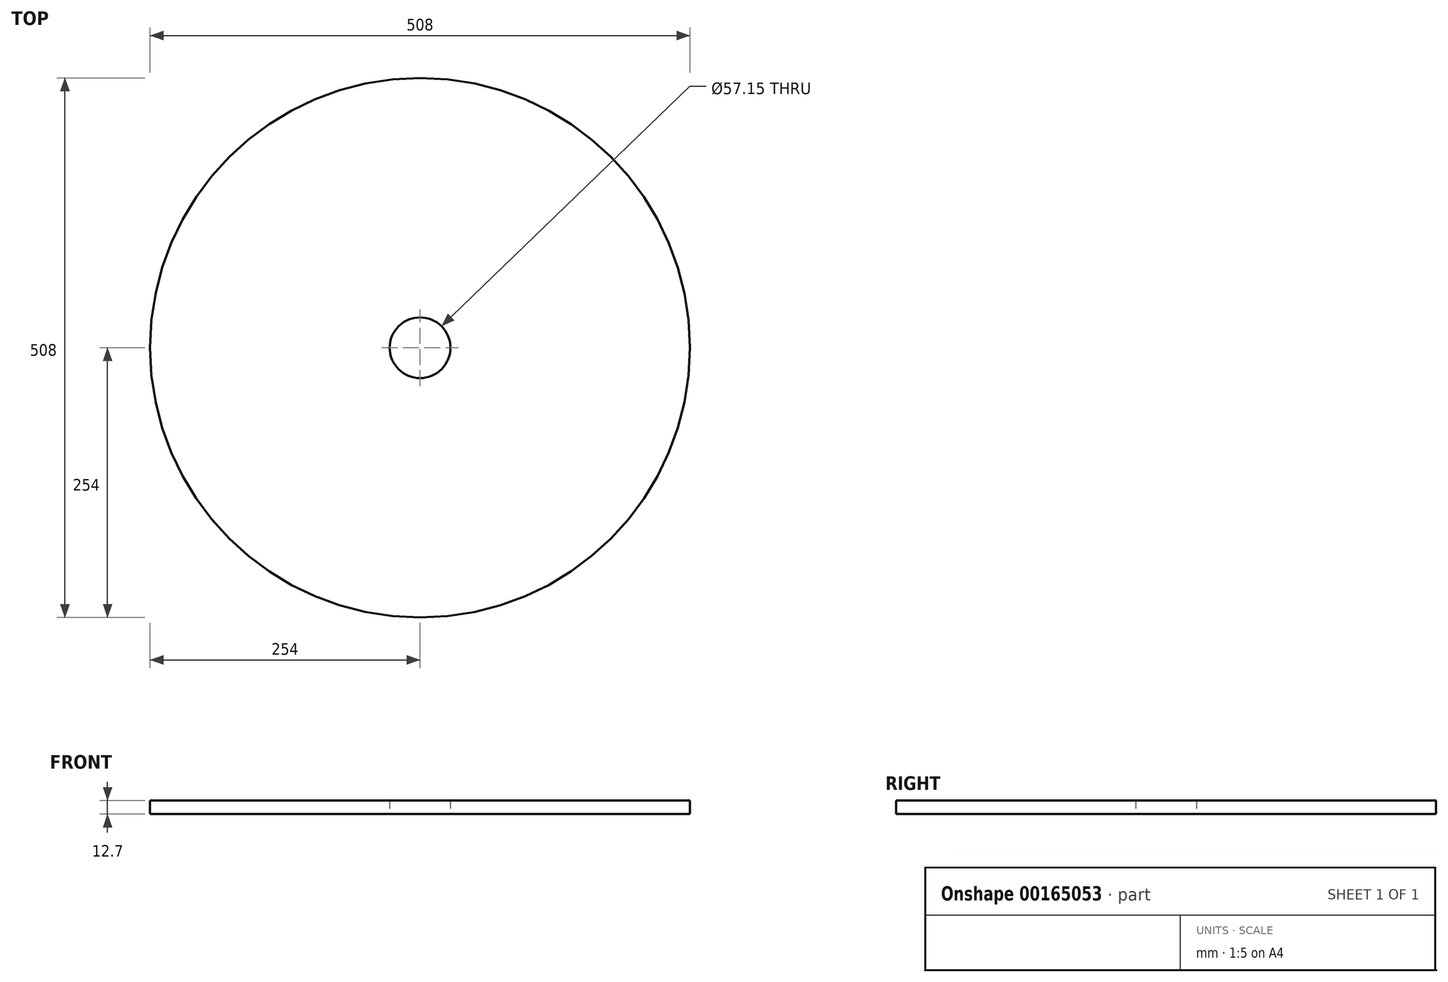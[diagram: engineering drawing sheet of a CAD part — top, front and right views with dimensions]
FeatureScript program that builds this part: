
annotation { "Feature Type Name" : "Feature", "Feature Type Description" : "" }
export const myFeature = defineFeature(function(context is Context, id is Id, definition is map)
    precondition{}
    {
        {
            var Q0;
            Q0=qCreatedBy(makeId("Top.planeOp"),FACE);
            var sketch = newSketch(context, id + "F0", { "sketchPlane" : qUnion([Q0])});
            skCircle(sketch, "E0", {"center": v(0, 0) * mm, "radius": 254 * mm});
            skCircle(sketch, "E1", {"center": v(0, 0) * mm, "radius": 28.58 * mm});
            skSolve(sketch);
        }
        {
            var Q0;
            Q0=qSketchRegion(id+"F0",true);
            extrude(context, id + "F1", {"entities" : qUnion([Q0]), "depth" : 12.7 * mm});
        }
    });
